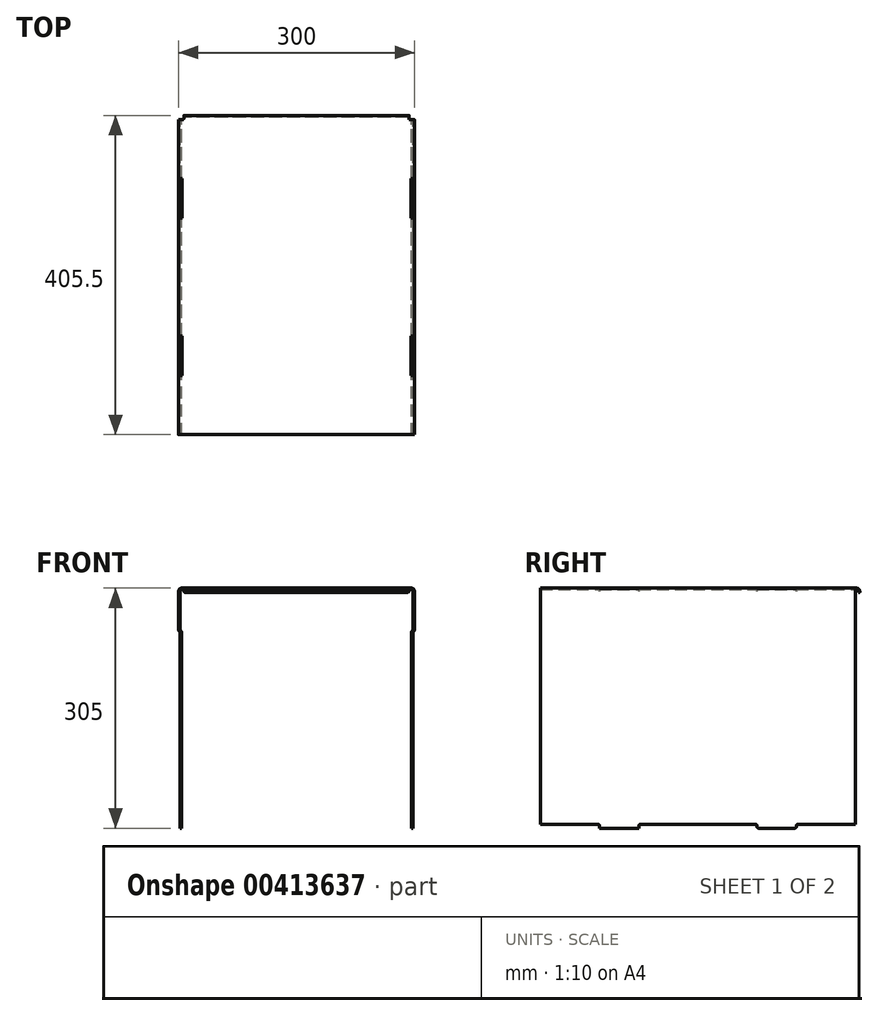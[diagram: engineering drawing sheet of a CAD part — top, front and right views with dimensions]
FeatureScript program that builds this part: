
annotation { "Feature Type Name" : "Feature", "Feature Type Description" : "" }
export const myFeature = defineFeature(function(context is Context, id is Id, definition is map)
    precondition{}
    {
        {
            var Q0;
            Q0=qCreatedBy(makeId("Front.planeOp"),FACE);
            var sketch = newSketch(context, id + "F0", { "sketchPlane" : qUnion([Q0])});
            skLineSegment(sketch, "E0.bottom", {"start": v(145.5, 152.5) * mm, "end": v(0, 152.5) * mm});
            skLineSegment(sketch, "E0.top", {"start": v(148, -152.5) * mm, "end": v(146, -152.5) * mm});
            skLineSegment(sketch, "E0.left", {"start": v(150, 148) * mm, "end": v(150, 100.5) * mm});
            skPoint(sketch, "E0.middle", {"position": v(0, 0) * mm});
            skLineSegment(sketch, "E1", {"start": v(148.95, 97.6) * mm, "end": v(148.58, 97.18) * mm});
            skLineSegment(sketch, "E2", {"start": v(148, 95.57) * mm, "end": v(148, -152.5) * mm});
            skPoint(sketch, "E3.visualSharp", {"position": v(150, 152.5) * mm});
            skArc(sketch, "E3.filletArc", {"start": v(150, 148) * mm, "mid": v(148.68, 151.18) * mm, "end": v(145.5, 152.5) * mm});
            skLineSegment(sketch, "E4", {"start": v(0, 150.5) * mm, "end": v(145.5, 150.5) * mm});
            skLineSegment(sketch, "E5.trimOffspring", {"start": v(148, 148) * mm, "end": v(148, 100.5) * mm});
            skPoint(sketch, "E6.visualSharp", {"position": v(148, 150.5) * mm});
            skArc(sketch, "E6.filletArc", {"start": v(148, 148) * mm, "mid": v(147.27, 149.77) * mm, "end": v(145.5, 150.5) * mm});
            skLineSegment(sketch, "E7", {"start": v(147.42, 98.9) * mm, "end": v(147.05, 98.46) * mm});
            skLineSegment(sketch, "E8", {"start": v(146, 95.57) * mm, "end": v(146, -152.5) * mm});
            skPoint(sketch, "E9.orphan", {"position": v(150, -152.5) * mm});
            skPoint(sketch, "E10.visualSharp", {"position": v(150, 98.86) * mm});
            skArc(sketch, "E10.filletArc", {"start": v(148.95, 97.6) * mm, "mid": v(149.73, 98.96) * mm, "end": v(150, 100.5) * mm});
            skPoint(sketch, "E11.visualSharp", {"position": v(148, 96.48) * mm});
            skArc(sketch, "E11.filletArc", {"start": v(148.58, 97.18) * mm, "mid": v(148.15, 96.42) * mm, "end": v(148, 95.57) * mm});
            skPoint(sketch, "E12.visualSharp", {"position": v(148, 99.6) * mm});
            skArc(sketch, "E12.filletArc", {"start": v(147.42, 98.9) * mm, "mid": v(147.85, 99.64) * mm, "end": v(148, 100.5) * mm});
            skPoint(sketch, "E13.visualSharp", {"position": v(146, 97.2) * mm});
            skArc(sketch, "E13.filletArc", {"start": v(147.05, 98.46) * mm, "mid": v(146.27, 97.1) * mm, "end": v(146, 95.57) * mm});
            skLineSegment(sketch, "E14", {"start": v(0, 0) * mm, "end": v(0, 158.87) * mm, "construction": true});
            skPoint(sketch, "E0.right.start.orphan", {"position": v(-150, 152.5) * mm});
            skLineSegment(sketch, "E15.MirrorCS", {"start": v(-145.5, 152.5) * mm, "end": v(0, 152.5) * mm});
            skLineSegment(sketch, "E16.MirrorCS", {"start": v(0, 150.5) * mm, "end": v(-145.5, 150.5) * mm});
            skArc(sketch, "E17.MirrorCS", {"start": v(-148, 148) * mm, "mid": v(-147.27, 149.77) * mm, "end": v(-145.5, 150.5) * mm});
            skArc(sketch, "E18.MirrorCS", {"start": v(-150, 148) * mm, "mid": v(-148.68, 151.18) * mm, "end": v(-145.5, 152.5) * mm});
            skLineSegment(sketch, "E19.MirrorCS", {"start": v(-148, 148) * mm, "end": v(-148, 100.5) * mm});
            skLineSegment(sketch, "E20.MirrorCS", {"start": v(-150, 148) * mm, "end": v(-150, 100.5) * mm});
            skLineSegment(sketch, "E21.MirrorCS", {"start": v(-148, 95.57) * mm, "end": v(-148, -152.5) * mm});
            skLineSegment(sketch, "E22.MirrorCS", {"start": v(-146, 95.57) * mm, "end": v(-146, -152.5) * mm});
            skArc(sketch, "E23.MirrorCS", {"start": v(-147.05, 98.46) * mm, "mid": v(-146.27, 97.1) * mm, "end": v(-146, 95.57) * mm});
            skArc(sketch, "E24.MirrorCS", {"start": v(-148.58, 97.18) * mm, "mid": v(-148.15, 96.42) * mm, "end": v(-148, 95.57) * mm});
            skArc(sketch, "E25.MirrorCS", {"start": v(-147.42, 98.9) * mm, "mid": v(-147.85, 99.64) * mm, "end": v(-148, 100.5) * mm});
            skArc(sketch, "E26.MirrorCS", {"start": v(-148.95, 97.6) * mm, "mid": v(-149.73, 98.96) * mm, "end": v(-150, 100.5) * mm});
            skLineSegment(sketch, "E27", {"start": v(-147.42, 98.9) * mm, "end": v(-147.05, 98.46) * mm});
            skLineSegment(sketch, "E28", {"start": v(-148.95, 97.6) * mm, "end": v(-148.58, 97.18) * mm});
            skLineSegment(sketch, "E29.trimOffspring", {"start": v(-146, -152.5) * mm, "end": v(-150, -152.5) * mm});
            skSolve(sketch);
        }
        {
            var Q0;
            Q0=qSketchRegion(id+"F0",true);
            extrude(context, id + "F1", {"entities" : qUnion([Q0]), "depth" : 400 * mm});
        }
        {
            var Q0;
            Q0=makeQuery(id+"F1.opExtrude","SWEPT_FACE",FACE,{"disambiguationData":[OSD([sQuery(id+"F0.wireOp",EDGE,"E2")])]});
            var sketch = newSketch(context, id + "F2", { "sketchPlane" : qUnion([Q0])});
            skLineSegment(sketch, "E30", {"start": v(-430.94, -147.5) * mm, "end": v(45.78, -147.5) * mm});
            skLineSegment(sketch, "E31.bottom", {"start": v(-400, -152.5) * mm, "end": v(-325, -152.5) * mm});
            skLineSegment(sketch, "E31.top", {"start": v(-400, -147.5) * mm, "end": v(-325, -147.5) * mm});
            skLineSegment(sketch, "E31.left", {"start": v(-400, -152.5) * mm, "end": v(-400, -147.5) * mm});
            skLineSegment(sketch, "E31.right", {"start": v(-325, -152.5) * mm, "end": v(-325, -147.5) * mm});
            skLineSegment(sketch, "E32.bottom", {"start": v(0, -152.5) * mm, "end": v(-75, -152.5) * mm});
            skLineSegment(sketch, "E32.top", {"start": v(0, -147.5) * mm, "end": v(-75, -147.5) * mm});
            skLineSegment(sketch, "E32.left", {"start": v(0, -152.5) * mm, "end": v(0, -147.5) * mm});
            skLineSegment(sketch, "E32.right", {"start": v(-75, -152.5) * mm, "end": v(-75, -147.5) * mm});
            skLineSegment(sketch, "E33", {"start": v(-200, 111) * mm, "end": v(-200, -165.3) * mm, "construction": true});
            skPoint(sketch, "E33.startSnap0", {"position": v(-200, 95.57) * mm});
            skLineSegment(sketch, "E34.bottom", {"start": v(-125, -147.5) * mm, "end": v(-275, -147.5) * mm, "construction": true});
            skLineSegment(sketch, "E34.top", {"start": v(-125, -164.16) * mm, "end": v(-275, -164.16) * mm, "construction": true});
            skLineSegment(sketch, "E34.left", {"start": v(-125, -147.5) * mm, "end": v(-125, -164.16) * mm});
            skLineSegment(sketch, "E34.right", {"start": v(-275, -147.5) * mm, "end": v(-275, -164.16) * mm});
            skPoint(sketch, "E34.middle", {"position": v(-200, -155.83) * mm});
            skSolve(sketch);
        }
        {
            var Q0;
            {var subQ0=sQuery(id+"F2.wireOp",EDGE,"E34.left");var subQ1=sQuery(id+"F2.wireOp",EDGE,"E30");var subQ2=makeQuery(id+"F2.imprint","INTERSECT",VERTEX,{"derivedFrom":[subQ1,subQ0]});Q0=makeQuery(id+"F2.imprint","IMPRINT",FACE,{"disambiguationData":[TD([[makeQuery(id+"F2.imprint","IMPRINT",EDGE,{"disambiguationData":[TD([[subQ2,1.0]])],"derivedFrom":subQ1}),-1.0]])]});}
            var Q1;
            Q1=makeQuery(id+"F2.imprint","IMPRINT",FACE,{"disambiguationData":[TD([[makeQuery(id+"F2.imprint","IMPRINT",EDGE,{"derivedFrom":sQuery(id+"F2.wireOp",EDGE,"E32.bottom")}),1.0]])]});
            var Q2;
            Q2=makeQuery(id+"F2.imprint","IMPRINT",FACE,{"disambiguationData":[TD([[makeQuery(id+"F2.imprint","IMPRINT",EDGE,{"derivedFrom":sQuery(id+"F2.wireOp",EDGE,"E31.bottom")}),1.0]])]});
            extrude(context, id + "F3", {"entities" : qUnion([Q0, Q1, Q2]), "operationType" : NewBodyOperationType.REMOVE, "oppositeDirection" : true, "depth" : 645 * mm});
        }
        {
            var Q0;
            Q0=makeQuery(id+"F1.opExtrude","SWEPT_FACE",FACE,{"disambiguationData":[OSD([sQuery(id+"F0.wireOp",EDGE,"E0.bottom"),sQuery(id+"F0.wireOp",EDGE,"E15.MirrorCS")])]});
            var sketch = newSketch(context, id + "F4", { "sketchPlane" : qUnion([Q0])});
            skLineSegment(sketch, "E35", {"start": v(-145.5, -200) * mm, "end": v(196.76, -200) * mm, "construction": true});
            skLineSegment(sketch, "E36", {"start": v(0, 0) * mm, "end": v(0, -263.53) * mm, "construction": true});
            skLineSegment(sketch, "E37.bottom", {"start": v(148, -125) * mm, "end": v(145.5, -125) * mm});
            skLineSegment(sketch, "E37.top", {"start": v(148, -75) * mm, "end": v(145.5, -75) * mm});
            skLineSegment(sketch, "E37.left", {"start": v(148, -125) * mm, "end": v(148, -75) * mm});
            skLineSegment(sketch, "E37.right", {"start": v(145.5, -125) * mm, "end": v(145.5, -75) * mm});
            skPoint(sketch, "E37.middle", {"position": v(146.75, -100) * mm});
            skLineSegment(sketch, "E38.MirrorCS", {"start": v(148, -325) * mm, "end": v(145.5, -325) * mm});
            skLineSegment(sketch, "E39.MirrorCS", {"start": v(145.5, -275) * mm, "end": v(145.5, -325) * mm});
            skLineSegment(sketch, "E40.MirrorCS", {"start": v(148, -275) * mm, "end": v(148, -325) * mm});
            skLineSegment(sketch, "E41.MirrorCS", {"start": v(148, -275) * mm, "end": v(145.5, -275) * mm});
            skLineSegment(sketch, "E42.MirrorCS", {"start": v(-148, -75) * mm, "end": v(-145.5, -75) * mm});
            skLineSegment(sketch, "E43.MirrorCS", {"start": v(-148, -125) * mm, "end": v(-145.5, -125) * mm});
            skLineSegment(sketch, "E44.MirrorCS", {"start": v(-145.5, -125) * mm, "end": v(-145.5, -75) * mm});
            skLineSegment(sketch, "E45.MirrorCS", {"start": v(-148, -125) * mm, "end": v(-148, -75) * mm});
            skPoint(sketch, "E46.MirrorP", {"position": v(-146.75, -100) * mm});
            skLineSegment(sketch, "E47.MirrorCS", {"start": v(-148, -325) * mm, "end": v(-145.5, -325) * mm});
            skLineSegment(sketch, "E48.MirrorCS", {"start": v(-148, -275) * mm, "end": v(-145.5, -275) * mm});
            skLineSegment(sketch, "E49.MirrorCS", {"start": v(-145.5, -275) * mm, "end": v(-145.5, -325) * mm});
            skLineSegment(sketch, "E50.MirrorCS", {"start": v(-148, -275) * mm, "end": v(-148, -325) * mm});
            skSolve(sketch);
        }
        {
            var Q0;
            Q0=makeQuery(id+"F4.imprint","IMPRINT",FACE,{"disambiguationData":[TD([[makeQuery(id+"F4.imprint","IMPRINT",EDGE,{"derivedFrom":sQuery(id+"F4.wireOp",EDGE,"E37.bottom")}),-1.0]])]});
            var Q1;
            Q1=makeQuery(id+"F4.imprint","IMPRINT",FACE,{"disambiguationData":[TD([[makeQuery(id+"F4.imprint","IMPRINT",EDGE,{"derivedFrom":sQuery(id+"F4.wireOp",EDGE,"E38.MirrorCS")}),-1.0]])]});
            var Q2;
            Q2=makeQuery(id+"F4.imprint","IMPRINT",FACE,{"disambiguationData":[TD([[makeQuery(id+"F4.imprint","IMPRINT",EDGE,{"derivedFrom":sQuery(id+"F4.wireOp",EDGE,"E42.MirrorCS")}),-1.0]])]});
            var Q3;
            Q3=makeQuery(id+"F4.imprint","IMPRINT",FACE,{"disambiguationData":[TD([[makeQuery(id+"F4.imprint","IMPRINT",EDGE,{"derivedFrom":sQuery(id+"F4.wireOp",EDGE,"E47.MirrorCS")}),1.0]])]});
            var Q4;
            Q4=sQuery(id+"F4.wireOp",EDGE,"E35");
            var Q5;
            Q5=sQuery(id+"F4.wireOp",EDGE,"E36");
            extrude(context, id + "F5", {"entities" : qUnion([Q0, Q1, Q2, Q3]), "operationType" : NewBodyOperationType.REMOVE, "surfaceEntities" : qUnion([Q4, Q5]), "oppositeDirection" : true, "depth" : 21 * mm});
        }
        {
            var Q0;
            {var subQ0=sQuery(id+"F2.wireOp",EDGE,"E30");var subQ1=sQuery(id+"F2.wireOp",EDGE,"E34.left");Q0=makeQuery(id+"F3.boolean.opBoolean","COPY",EDGE,{"disambiguationData":[TD([makeQuery(id+"F1.opExtrude","SWEPT_FACE",FACE,{"disambiguationData":[OSD([sQuery(id+"F0.wireOp",EDGE,"E2")])]})])],"derivedFrom":makeQuery(id+"F3.opExtrude","SWEPT_EDGE",EDGE,{"disambiguationData":[OSD([subQ0,subQ1])]})});}
            var Q1;
            {var subQ0=sQuery(id+"F2.wireOp",EDGE,"E31.right");var subQ1=sQuery(id+"F2.wireOp",EDGE,"E31.top");Q1=makeQuery(id+"F3.boolean.opBoolean","COPY",EDGE,{"disambiguationData":[TD([makeQuery(id+"F1.opExtrude","SWEPT_FACE",FACE,{"disambiguationData":[OSD([sQuery(id+"F0.wireOp",EDGE,"E2")])]})])],"derivedFrom":makeQuery(id+"F3.opExtrude","SWEPT_EDGE",EDGE,{"disambiguationData":[OSD([sQuery(id+"F2.wireOp",EDGE,"E30"),subQ1,subQ0])]})});}
            var Q2;
            {var subQ0=sQuery(id+"F2.wireOp",EDGE,"E31.right");var subQ1=sQuery(id+"F2.wireOp",EDGE,"E31.top");Q2=makeQuery(id+"F3.boolean.opBoolean","COPY",EDGE,{"disambiguationData":[TD([makeQuery(id+"F1.opExtrude","SWEPT_FACE",FACE,{"disambiguationData":[OSD([sQuery(id+"F0.wireOp",EDGE,"E21.MirrorCS")])]})])],"derivedFrom":makeQuery(id+"F3.opExtrude","SWEPT_EDGE",EDGE,{"disambiguationData":[OSD([sQuery(id+"F2.wireOp",EDGE,"E30"),subQ1,subQ0])]})});}
            var Q3;
            {var subQ0=sQuery(id+"F2.wireOp",EDGE,"E30");var subQ1=sQuery(id+"F2.wireOp",EDGE,"E34.left");Q3=makeQuery(id+"F3.boolean.opBoolean","COPY",EDGE,{"disambiguationData":[TD([makeQuery(id+"F1.opExtrude","SWEPT_FACE",FACE,{"disambiguationData":[OSD([sQuery(id+"F0.wireOp",EDGE,"E21.MirrorCS")])]})])],"derivedFrom":makeQuery(id+"F3.opExtrude","SWEPT_EDGE",EDGE,{"disambiguationData":[OSD([subQ0,subQ1])]})});}
            var Q4;
            {var subQ0=sQuery(id+"F2.wireOp",EDGE,"E32.right");var subQ1=sQuery(id+"F2.wireOp",EDGE,"E32.top");Q4=makeQuery(id+"F3.boolean.opBoolean","COPY",EDGE,{"disambiguationData":[TD([makeQuery(id+"F1.opExtrude","SWEPT_FACE",FACE,{"disambiguationData":[OSD([sQuery(id+"F0.wireOp",EDGE,"E2")])]})])],"derivedFrom":makeQuery(id+"F3.opExtrude","SWEPT_EDGE",EDGE,{"disambiguationData":[OSD([sQuery(id+"F2.wireOp",EDGE,"E30"),subQ1,subQ0])]})});}
            var Q5;
            {var subQ0=sQuery(id+"F2.wireOp",EDGE,"E30");var subQ1=sQuery(id+"F2.wireOp",EDGE,"E34.right");Q5=makeQuery(id+"F3.boolean.opBoolean","COPY",EDGE,{"disambiguationData":[TD([makeQuery(id+"F1.opExtrude","SWEPT_FACE",FACE,{"disambiguationData":[OSD([sQuery(id+"F0.wireOp",EDGE,"E2")])]})])],"derivedFrom":makeQuery(id+"F3.opExtrude","SWEPT_EDGE",EDGE,{"disambiguationData":[OSD([subQ0,subQ1])]})});}
            var Q6;
            {var subQ0=sQuery(id+"F2.wireOp",EDGE,"E30");var subQ1=sQuery(id+"F2.wireOp",EDGE,"E34.right");Q6=makeQuery(id+"F3.boolean.opBoolean","COPY",EDGE,{"disambiguationData":[TD([makeQuery(id+"F1.opExtrude","SWEPT_FACE",FACE,{"disambiguationData":[OSD([sQuery(id+"F0.wireOp",EDGE,"E21.MirrorCS")])]})])],"derivedFrom":makeQuery(id+"F3.opExtrude","SWEPT_EDGE",EDGE,{"disambiguationData":[OSD([subQ0,subQ1])]})});}
            var Q7;
            {var subQ0=sQuery(id+"F2.wireOp",EDGE,"E32.right");var subQ1=sQuery(id+"F2.wireOp",EDGE,"E32.top");Q7=makeQuery(id+"F3.boolean.opBoolean","COPY",EDGE,{"disambiguationData":[TD([makeQuery(id+"F1.opExtrude","SWEPT_FACE",FACE,{"disambiguationData":[OSD([sQuery(id+"F0.wireOp",EDGE,"E21.MirrorCS")])]})])],"derivedFrom":makeQuery(id+"F3.opExtrude","SWEPT_EDGE",EDGE,{"disambiguationData":[OSD([sQuery(id+"F2.wireOp",EDGE,"E30"),subQ1,subQ0])]})});}
            var Q8;
            {var subQ0=sQuery(id+"F0.wireOp",EDGE,"E0.top");var subQ1=sQuery(id+"F2.wireOp",EDGE,"E31.right");Q8=makeQuery(id+"F3.boolean.opBoolean","COPY",EDGE,{"disambiguationData":[topologyDisambiguationEdgeConnected([makeQuery(id+"F1.opExtrude","SWEPT_FACE",FACE,{"disambiguationData":[OSD([subQ0])]})])],"derivedFrom":makeQuery(id+"F3.opExtrude","SWEPT_EDGE",EDGE,{"disambiguationData":[OSD([subQ0,sQuery(id+"F0.wireOp",EDGE,"E2"),sQuery(id+"F2.wireOp",EDGE,"E31.bottom"),subQ1])]})});}
            var Q9;
            {var subQ0=sQuery(id+"F0.wireOp",EDGE,"E0.top");var subQ1=sQuery(id+"F2.wireOp",EDGE,"E34.left");Q9=makeQuery(id+"F3.boolean.opBoolean","COPY",EDGE,{"disambiguationData":[topologyDisambiguationEdgeConnected([makeQuery(id+"F1.opExtrude","SWEPT_FACE",FACE,{"disambiguationData":[OSD([subQ0])]})])],"derivedFrom":makeQuery(id+"F3.opExtrude","SWEPT_EDGE",EDGE,{"disambiguationData":[OSD([subQ0,sQuery(id+"F0.wireOp",EDGE,"E2"),subQ1])]})});}
            var Q10;
            {var subQ0=sQuery(id+"F2.wireOp",EDGE,"E31.right");Q10=makeQuery(id+"F3.boolean.opBoolean","COPY",EDGE,{"disambiguationData":[topologyDisambiguationEdgeConnected([makeQuery(id+"F1.opExtrude","SWEPT_FACE",FACE,{"disambiguationData":[OSD([sQuery(id+"F0.wireOp",EDGE,"E29.trimOffspring")])]})])],"derivedFrom":makeQuery(id+"F3.opExtrude","SWEPT_EDGE",EDGE,{"disambiguationData":[OSD([sQuery(id+"F0.wireOp",EDGE,"E0.top"),sQuery(id+"F0.wireOp",EDGE,"E2"),sQuery(id+"F2.wireOp",EDGE,"E31.bottom"),subQ0])]})});}
            var Q11;
            {var subQ0=sQuery(id+"F2.wireOp",EDGE,"E34.left");Q11=makeQuery(id+"F3.boolean.opBoolean","COPY",EDGE,{"disambiguationData":[topologyDisambiguationEdgeConnected([makeQuery(id+"F1.opExtrude","SWEPT_FACE",FACE,{"disambiguationData":[OSD([sQuery(id+"F0.wireOp",EDGE,"E29.trimOffspring")])]})])],"derivedFrom":makeQuery(id+"F3.opExtrude","SWEPT_EDGE",EDGE,{"disambiguationData":[OSD([sQuery(id+"F0.wireOp",EDGE,"E0.top"),sQuery(id+"F0.wireOp",EDGE,"E2"),subQ0])]})});}
            var Q12;
            {var subQ0=sQuery(id+"F0.wireOp",EDGE,"E0.top");var subQ1=sQuery(id+"F2.wireOp",EDGE,"E34.right");Q12=makeQuery(id+"F3.boolean.opBoolean","COPY",EDGE,{"disambiguationData":[topologyDisambiguationEdgeConnected([makeQuery(id+"F1.opExtrude","SWEPT_FACE",FACE,{"disambiguationData":[OSD([subQ0])]})])],"derivedFrom":makeQuery(id+"F3.opExtrude","SWEPT_EDGE",EDGE,{"disambiguationData":[OSD([subQ0,sQuery(id+"F0.wireOp",EDGE,"E2"),subQ1])]})});}
            var Q13;
            {var subQ0=sQuery(id+"F0.wireOp",EDGE,"E0.top");var subQ1=sQuery(id+"F2.wireOp",EDGE,"E32.right");Q13=makeQuery(id+"F3.boolean.opBoolean","COPY",EDGE,{"disambiguationData":[topologyDisambiguationEdgeConnected([makeQuery(id+"F1.opExtrude","SWEPT_FACE",FACE,{"disambiguationData":[OSD([subQ0])]})])],"derivedFrom":makeQuery(id+"F3.opExtrude","SWEPT_EDGE",EDGE,{"disambiguationData":[OSD([subQ0,sQuery(id+"F0.wireOp",EDGE,"E2"),sQuery(id+"F2.wireOp",EDGE,"E32.bottom"),subQ1])]})});}
            var Q14;
            {var subQ0=sQuery(id+"F2.wireOp",EDGE,"E34.right");Q14=makeQuery(id+"F3.boolean.opBoolean","COPY",EDGE,{"disambiguationData":[topologyDisambiguationEdgeConnected([makeQuery(id+"F1.opExtrude","SWEPT_FACE",FACE,{"disambiguationData":[OSD([sQuery(id+"F0.wireOp",EDGE,"E29.trimOffspring")])]})])],"derivedFrom":makeQuery(id+"F3.opExtrude","SWEPT_EDGE",EDGE,{"disambiguationData":[OSD([sQuery(id+"F0.wireOp",EDGE,"E0.top"),sQuery(id+"F0.wireOp",EDGE,"E2"),subQ0])]})});}
            var Q15;
            {var subQ0=sQuery(id+"F2.wireOp",EDGE,"E32.right");Q15=makeQuery(id+"F3.boolean.opBoolean","COPY",EDGE,{"disambiguationData":[topologyDisambiguationEdgeConnected([makeQuery(id+"F1.opExtrude","SWEPT_FACE",FACE,{"disambiguationData":[OSD([sQuery(id+"F0.wireOp",EDGE,"E29.trimOffspring")])]})])],"derivedFrom":makeQuery(id+"F3.opExtrude","SWEPT_EDGE",EDGE,{"disambiguationData":[OSD([sQuery(id+"F0.wireOp",EDGE,"E0.top"),sQuery(id+"F0.wireOp",EDGE,"E2"),sQuery(id+"F2.wireOp",EDGE,"E32.bottom"),subQ0])]})});}
            fillet(context, id + "F6", {"entities" : qUnion([Q0, Q1, Q2, Q3, Q4, Q5, Q6, Q7, Q8, Q9, Q10, Q11, Q12, Q13, Q14, Q15]), "radius" : 2 * mm, "tangentPropagation" : true, "allowEdgeOverflow" : false});
        }
        {
            var Q0;
            Q0=qCreatedBy(makeId("Right.planeOp"),FACE);
            var sketch = newSketch(context, id + "F7", { "sketchPlane" : qUnion([Q0])});
            skLineSegment(sketch, "E51", {"start": v(0, 152.5) * mm, "end": v(1, 152.5) * mm});
            skLineSegment(sketch, "E52", {"start": v(5.5, 148) * mm, "end": v(5.5, 147) * mm});
            skLineSegment(sketch, "E53", {"start": v(5.5, 147) * mm, "end": v(3.5, 147) * mm});
            skLineSegment(sketch, "E54", {"start": v(3.5, 147) * mm, "end": v(3.5, 148) * mm});
            skLineSegment(sketch, "E55", {"start": v(1, 150.5) * mm, "end": v(0, 150.5) * mm});
            skLineSegment(sketch, "E56", {"start": v(0, 150.5) * mm, "end": v(0, 152.5) * mm});
            skPoint(sketch, "E57.visualSharp", {"position": v(5.5, 152.5) * mm});
            skArc(sketch, "E57.filletArc", {"start": v(5.5, 148) * mm, "mid": v(4.18, 151.18) * mm, "end": v(1, 152.5) * mm});
            skPoint(sketch, "E58.visualSharp", {"position": v(3.5, 150.5) * mm});
            skArc(sketch, "E58.filletArc", {"start": v(3.5, 148) * mm, "mid": v(2.77, 149.77) * mm, "end": v(1, 150.5) * mm});
            skSolve(sketch);
        }
        {
            var Q0;
            Q0=makeQuery(id+"F7.imprint","IMPRINT",FACE,{"disambiguationData":[TD([[makeQuery(id+"F7.imprint","IMPRINT",EDGE,{"derivedFrom":sQuery(id+"F7.wireOp",EDGE,"E51")}),-1.0]])]});
            var Q1;
            Q1=makeQuery(id+"F1.opExtrude","CAP_VERTEX",VERTEX,{"disambiguationData":[OSD([sQuery(id+"F0.wireOp",EDGE,"E0.bottom"),sQuery(id+"F0.wireOp",EDGE,"E3.filletArc")])],"isStart":true});
            var Q2;
            Q2=sQuery(id+"F7.wireOp",VERTEX,"E58.filletArc.end");
            extrude(context, id + "F8", {"entities" : qUnion([Q0]), "operationType" : NewBodyOperationType.ADD, "endBoundEntityVertex" : qUnion([Q1]), "depth" : 143 * mm, "hasSecondDirection" : true, "secondDirectionOppositeDirection" : true, "secondDirectionBoundEntityVertex" : qUnion([Q2]), "secondDirectionDepth" : 143 * mm});
        }
        {
            var Q0;
            Q0=makeQuery(id+"F8.opExtrude","CAP_EDGE",EDGE,{"disambiguationData":[OSD([sQuery(id+"F7.wireOp",EDGE,"E56")])],"isStart":false});
            var Q1;
            Q1=makeQuery(id+"F8.opExtrude","CAP_EDGE",EDGE,{"disambiguationData":[OSD([sQuery(id+"F7.wireOp",EDGE,"E56")])],"isStart":true});
            var Q2;
            Q2=makeQuery(id+"F8.opExtrude","CAP_EDGE",EDGE,{"disambiguationData":[OSD([sQuery(id+"F7.wireOp",EDGE,"E53")])],"isStart":true});
            var Q3;
            Q3=makeQuery(id+"F8.opExtrude","CAP_EDGE",EDGE,{"disambiguationData":[OSD([sQuery(id+"F7.wireOp",EDGE,"E53")])],"isStart":false});
            fillet(context, id + "F9", {"entities" : qUnion([Q0, Q1, Q2, Q3]), "radius" : 2 * mm, "tangentPropagation" : true, "allowEdgeOverflow" : false});
        }
    });
